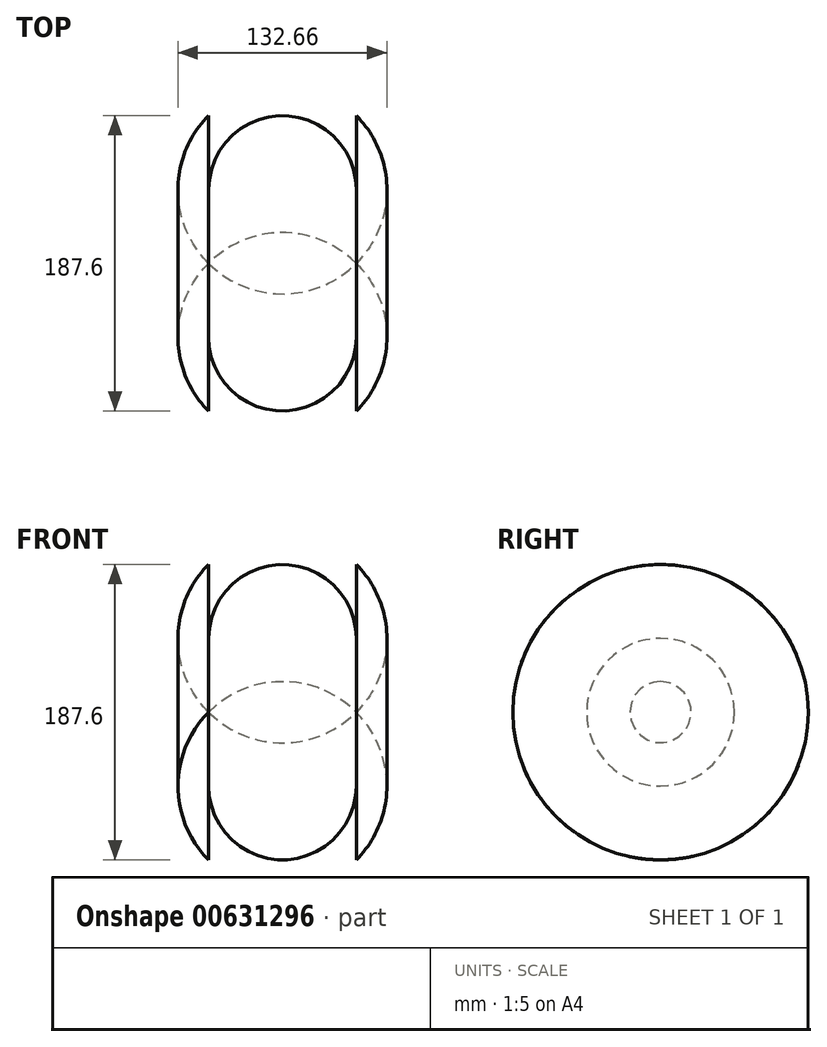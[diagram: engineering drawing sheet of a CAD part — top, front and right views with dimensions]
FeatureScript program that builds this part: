
annotation { "Feature Type Name" : "Feature", "Feature Type Description" : "" }
export const myFeature = defineFeature(function(context is Context, id is Id, definition is map)
    precondition{}
    {
        {
            var Q0;
            Q0=qCreatedBy(makeId("Top.planeOp"),FACE);
            var sketch = newSketch(context, id + "F0", { "sketchPlane" : qUnion([Q0])});
            skLineSegment(sketch, "E0.bottom", {"start": v(66.33, 66.33) * mm, "end": v(-66.33, 66.33) * mm});
            skLineSegment(sketch, "E0.top", {"start": v(66.33, -66.33) * mm, "end": v(-66.33, -66.33) * mm});
            skLineSegment(sketch, "E0.left", {"start": v(66.33, 66.33) * mm, "end": v(66.33, -66.33) * mm});
            skLineSegment(sketch, "E0.right", {"start": v(-66.33, 66.33) * mm, "end": v(-66.33, -66.33) * mm});
            skPoint(sketch, "E0.middle", {"position": v(0, 0) * mm});
            skCircle(sketch, "E1", {"center": v(0, 0) * mm, "radius": 66.33 * mm});
            skLineSegment(sketch, "E2.bottom", {"start": v(46.9, 46.9) * mm, "end": v(-46.9, 46.9) * mm});
            skLineSegment(sketch, "E2.top", {"start": v(46.9, -46.9) * mm, "end": v(-46.9, -46.9) * mm});
            skLineSegment(sketch, "E2.left", {"start": v(46.9, 46.9) * mm, "end": v(46.9, -46.9) * mm});
            skLineSegment(sketch, "E2.right", {"start": v(-46.9, 46.9) * mm, "end": v(-46.9, -46.9) * mm});
            skCircle(sketch, "E3", {"center": v(0, 0) * mm, "radius": 46.9 * mm});
            skSolve(sketch);
        }
        {
            var Q0;
            {var subQ1=sQuery(id+"F0.wireOp",EDGE,"E2.bottom");var subQ3=sQuery(id+"F0.wireOp",EDGE,"E3");var subQ4=makeQuery(id+"F0.imprint","INTERSECT",VERTEX,{"derivedFrom":[subQ1,subQ3]});Q0=makeQuery(id+"F0.imprint","IMPRINT",FACE,{"disambiguationData":[TD([[makeQuery(id+"F0.imprint","IMPRINT",EDGE,{"disambiguationData":[TD([[subQ4,1.0]])],"derivedFrom":subQ3}),-1.0]])]});}
            var Q1;
            {var subQ1=sQuery(id+"F0.wireOp",EDGE,"E1");var subQ3=makeQuery(id+"F0.imprint","INTERSECT",VERTEX,{"derivedFrom":[sQuery(id+"F0.wireOp",EDGE,"E0.bottom"),subQ1]});Q1=makeQuery(id+"F0.imprint","IMPRINT",FACE,{"disambiguationData":[TD([[makeQuery(id+"F0.imprint","IMPRINT",EDGE,{"disambiguationData":[TD([[subQ3,1.0]])],"derivedFrom":subQ1}),1.0]])]});}
            var Q2;
            {var subQ1=sQuery(id+"F0.wireOp",EDGE,"E2.bottom");var subQ3=sQuery(id+"F0.wireOp",EDGE,"E3");var subQ4=makeQuery(id+"F0.imprint","INTERSECT",VERTEX,{"derivedFrom":[subQ1,subQ3]});Q2=makeQuery(id+"F0.imprint","IMPRINT",FACE,{"disambiguationData":[TD([[makeQuery(id+"F0.imprint","IMPRINT",EDGE,{"disambiguationData":[TD([[subQ4,-1.0]])],"derivedFrom":subQ3}),-1.0]])]});}
            var Q3;
            Q3=sQuery(id+"F0.wireOp",EDGE,"E2.top");
            revolve(context, id + "F1", {"entities" : qUnion([Q0, Q1, Q2]), "axis" : qUnion([Q3]), "revolveType" : RevolveType.FULL});
        }
    });
